# Revit family: 205_SLCU50 900
name_source: partatom
category: Duct Accessories
revit_build: Autodesk Revit 2018 (Build: 20170223_1515(x64)
units: mm (PartAtom-declared; Revit-internal decimal feet)

## family parameters
Always vertical = Yes
Cut with Voids When Loaded = No
Part Type = Breaks Into
Round Connector Dimension = Use Diameter
Shared = No
Work Plane-Based = No

## types (1)
- 200-12524
    CAT0 = Yes
    D = 200 mm
    D1 = 325 mm  [stored 1.06627 ft]
    D2 = 286 mm  [stored 0.93832 ft]
    Description = Silencer steel 0,9m
    H2D = 324 mm
    L1 = 10 mm  [stored 0.0328084 ft]
    L1__ve = -10 mm  [stored -0.0328084 ft]
    L2 = 20 mm  [stored 0.0656168 ft]
    L22 = 450 mm  [stored 1.47638 ft]
    L2D = 900 mm
    LL = 840 mm  [stored 2.75591 ft]
    MC Product Code = 200-12524
    Manufacturer = Flexit
    QmdConnectorList = 201;D;202;D
    R = 100 mm  [stored 0.328084 ft]
    URL = www.flexit.no
    W2D = 324 mm
    magiPartTypeId = 205
    magiProductFamilyId = SLCU50 900
    magiProductId = SLCU 200 900 50

note: [stored X ft] marks values corroborated as IEEE doubles in the binary element streams (Revit-internal decimal feet)

## geometry (parser evidence)
native form markers: Sweep x2
no freeform markers — native parametric forms only
